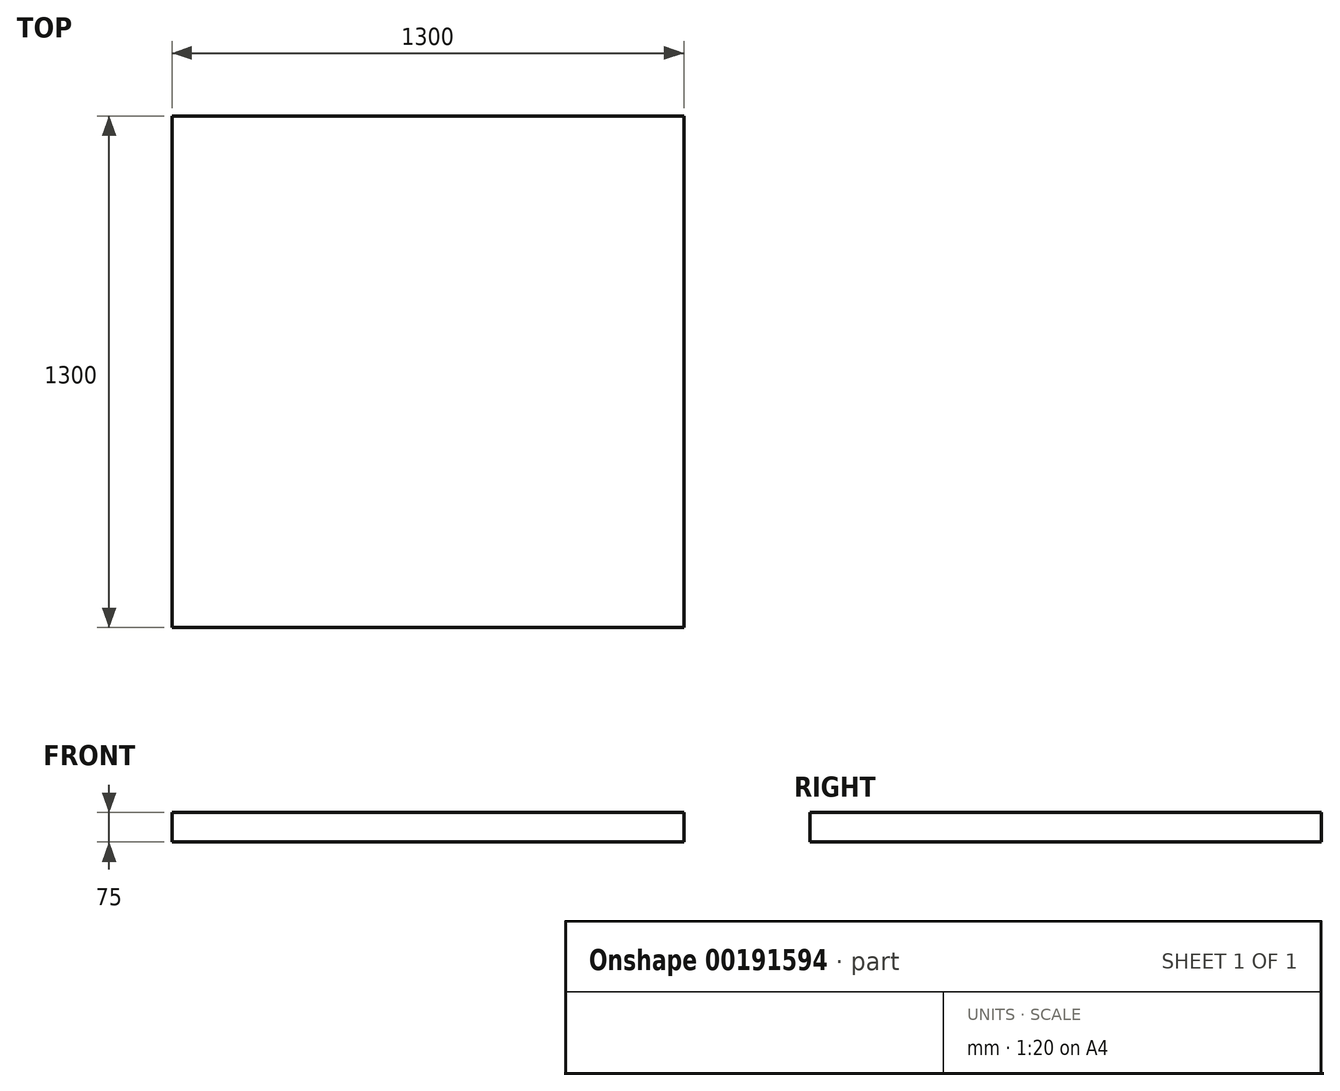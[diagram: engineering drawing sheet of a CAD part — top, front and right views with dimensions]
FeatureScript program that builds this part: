
annotation { "Feature Type Name" : "Feature", "Feature Type Description" : "" }
export const myFeature = defineFeature(function(context is Context, id is Id, definition is map)
    precondition{}
    {
        {
            var Q0;
            Q0=qCreatedBy(makeId("Top.planeOp"),FACE);
            var sketch = newSketch(context, id + "F0", { "sketchPlane" : qUnion([Q0])});
            skLineSegment(sketch, "E0.bottom", {"start": v(-650, -650) * mm, "end": v(650, -650) * mm});
            skLineSegment(sketch, "E0.top", {"start": v(-650, 650) * mm, "end": v(650, 650) * mm});
            skLineSegment(sketch, "E0.left", {"start": v(-650, 650) * mm, "end": v(-650, -650) * mm});
            skLineSegment(sketch, "E0.right", {"start": v(650, 650) * mm, "end": v(650, -650) * mm});
            skLineSegment(sketch, "E1", {"start": v(-650, -650) * mm, "end": v(650, 650) * mm, "construction": true});
            skLineSegment(sketch, "E2", {"start": v(-650, 650) * mm, "end": v(650, -650) * mm, "construction": true});
            skSolve(sketch);
        }
        {
            var Q0;
            Q0 = qSketchRegion(id + "F0", true);
            extrude(context, id + "F1", {"entities" : qUnion([Q0]), "depth" : 75 * mm});
        }
    });
